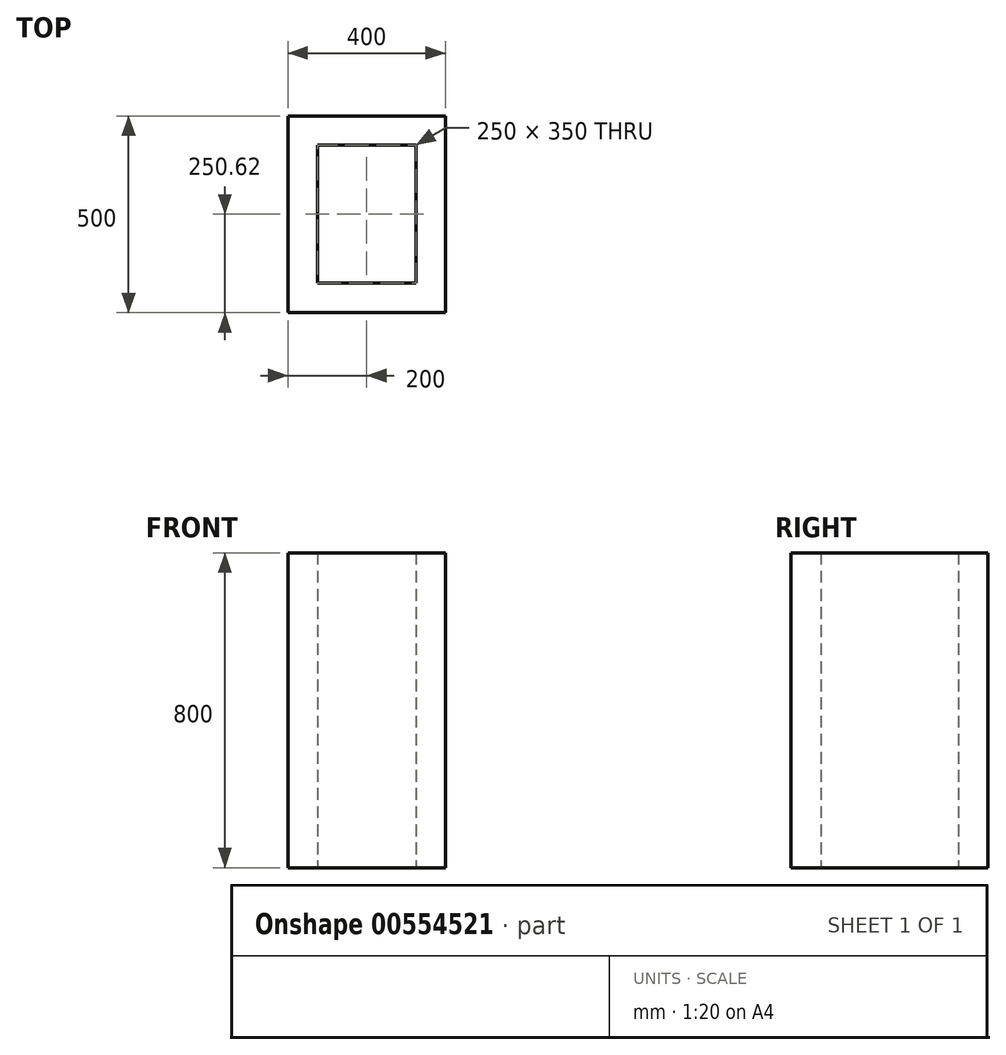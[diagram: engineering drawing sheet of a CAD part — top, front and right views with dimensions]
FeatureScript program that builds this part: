
annotation { "Feature Type Name" : "Feature", "Feature Type Description" : "" }
export const myFeature = defineFeature(function(context is Context, id is Id, definition is map)
    precondition{}
    {
        {
            var Q0;
            Q0=qCreatedBy(makeId("Top.planeOp"),FACE);
            var sketch = newSketch(context, id + "F0", { "sketchPlane" : qUnion([Q0])});
            skLineSegment(sketch, "E0.bottom", {"start": v(200, -250.62) * mm, "end": v(-200, -250.62) * mm});
            skLineSegment(sketch, "E0.top", {"start": v(200, 249.38) * mm, "end": v(-200, 249.38) * mm});
            skLineSegment(sketch, "E0.left", {"start": v(200, -250.62) * mm, "end": v(200, 249.38) * mm});
            skLineSegment(sketch, "E0.right", {"start": v(-200, -250.62) * mm, "end": v(-200, 249.38) * mm});
            skPoint(sketch, "E0.middle", {"position": v(0, -0.62) * mm});
            skPoint(sketch, "E1.middle", {"position": v(0, 0) * mm});
            skLineSegment(sketch, "E2.bottom", {"start": v(125, -175) * mm, "end": v(-125, -175) * mm});
            skLineSegment(sketch, "E2.top", {"start": v(125, 175) * mm, "end": v(-125, 175) * mm});
            skLineSegment(sketch, "E2.left", {"start": v(125, -175) * mm, "end": v(125, 175) * mm});
            skLineSegment(sketch, "E2.right", {"start": v(-125, -175) * mm, "end": v(-125, 175) * mm});
            skSolve(sketch);
        }
        {
            var Q0;
            Q0=makeQuery(id+"F0.imprint","IMPRINT",FACE,{"disambiguationData":[TD([[makeQuery(id+"F0.imprint","IMPRINT",EDGE,{"derivedFrom":sQuery(id+"F0.wireOp",EDGE,"E0.bottom")}),-1.0]])]});
            extrude(context, id + "F1", {"entities" : qUnion([Q0]), "depth" : 800 * mm, "offsetDistance" : 25 * mm});
        }
    });
